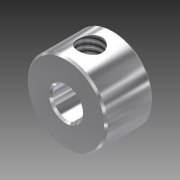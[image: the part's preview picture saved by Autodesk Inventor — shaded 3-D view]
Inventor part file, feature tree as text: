
AUTODESK INVENTOR PART (.ipt)
format: ipt  version: 2013 (Build 170138000, 138)  size: 116,736 bytes
history: native  units: in
note: dims shown in document units (in); Inventor stores cm internally (conversion verified against a paired STEP export)
features: sketch x3, chamfer x2, hole x2, extrude x1, plane x1
ambient origin geometry x8: Origin, YZ Plane, XZ Plane, XY Plane, X Axis, Y Axis, Z Axis, Center Point
bodies: Solid1 (feature_tree)
feature tree (9):
  extrude  "Extrusion1"  Depth=0.26in TaperAngle=0.0deg
  chamfer  "Chamfer1"  Distance=0.01in Angle=45.0deg
  hole  "Hole1"  [1 undecoded]
  plane  "Work Plane1"
  hole  "Hole2"  [1 undecoded]
  chamfer  "Chamfer2"  [1 undecoded]
  sketch  "Sketch1"  dims[d0=0.433in d1=0.26in d2=0.0in d3=0.01in d4=0.125in d5=45.0deg]
  sketch  "Sketch2"  dims[d6=0.165in d7=0.75in d8=0.375in d9=0.25in d10=0.5635in d11=1.0in d12=0.8108in]
  sketch  "Sketch3"  dims[d13=0.13in d14=0.75in d15=0.375in d16=0.25in d17=0.5635in d18=1.0in d19=0.8108in d20=0.01in d21=0.125in d22=45.0deg]
note: 3 required parameter values undecoded (feature->parameter linkage not recoverable at this tier; creation-order binding heuristic only, values carry confidence <= 0.55)
